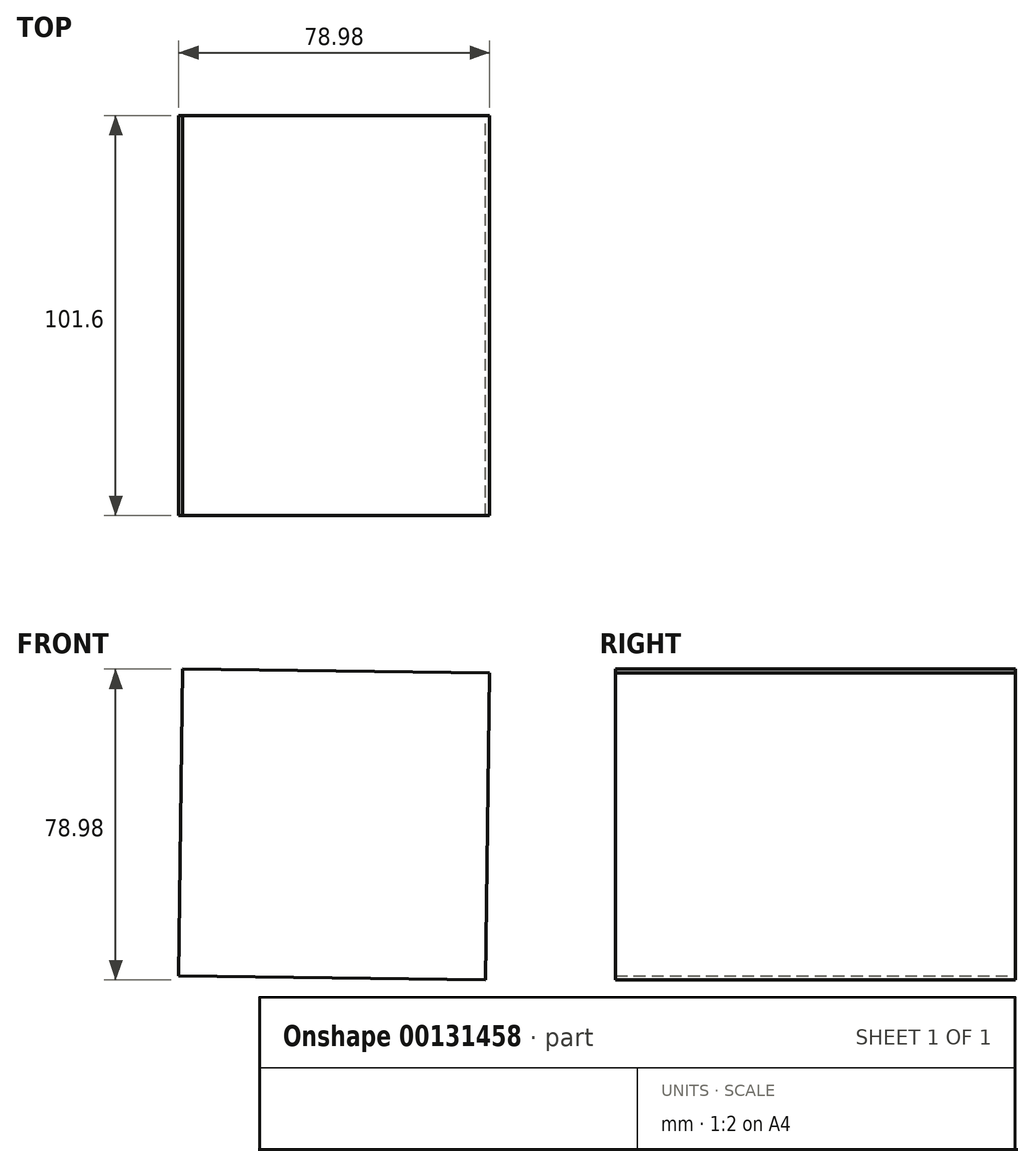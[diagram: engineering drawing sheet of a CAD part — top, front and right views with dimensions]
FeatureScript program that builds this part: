
annotation { "Feature Type Name" : "Feature", "Feature Type Description" : "" }
export const myFeature = defineFeature(function(context is Context, id is Id, definition is map)
    precondition{}
    {
        {
            var Q0;
            Q0=qCreatedBy(makeId("Front.planeOp"),FACE);
            var sketch = newSketch(context, id + "F0", { "sketchPlane" : qUnion([Q0])});
            skCircle(sketch, "E0.cCircle", {"center": v(0, 0) * mm, "radius": 55.14 * mm, "construction": true});
            skLineSegment(sketch, "E0.0", {"start": v(38.47, -39.5) * mm, "end": v(-39.5, -38.47) * mm});
            skLineSegment(sketch, "E0.1", {"start": v(-39.5, -38.47) * mm, "end": v(-38.47, 39.5) * mm});
            skLineSegment(sketch, "E0.2", {"start": v(-38.47, 39.5) * mm, "end": v(39.5, 38.47) * mm});
            skLineSegment(sketch, "E0.3", {"start": v(39.5, 38.47) * mm, "end": v(38.47, -39.5) * mm});
            skSolve(sketch);
        }
        {
            var Q0;
            Q0=makeQuery(id+"F0.imprint","IMPRINT",FACE,{"disambiguationData":[TD([[makeQuery(id+"F0.imprint","IMPRINT",EDGE,{"derivedFrom":sQuery(id+"F0.wireOp",EDGE,"E0.0")}),-1.0]])]});
            extrude(context, id + "F1", {"entities" : qUnion([Q0]), "depth" : 101.6 * mm});
        }
    });
